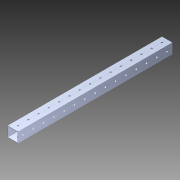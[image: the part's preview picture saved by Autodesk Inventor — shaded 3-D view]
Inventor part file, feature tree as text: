
AUTODESK INVENTOR PART (.ipt)
format: ipt  version: 2014 (Build 180170000, 170)  size: 1,226,752 bytes
history: native  units: in
note: dims shown in document units (in); Inventor stores cm internally (conversion verified against a paired STEP export)
features: pattern_circular x1, other x1, plane x1, extrude x1, imported_body x1, sketch x1
ambient origin geometry x8: Origin, YZ Plane, XZ Plane, XY Plane, X Axis, Y Axis, Z Axis, Center Point
bodies: Body1 (feature_tree)
feature tree (6):
  pattern_circular  "CirPattern2"
  other  "217-3426-STEP1"
  plane  "Work Plane1"
  extrude  "Extrusion1"  Depth=3937.0079in TaperAngle=0.0deg
  imported_body  "Base1"
  sketch  "Sketch1"  dims[d0=-15.0in d1=3937.0079in d2=0.0in]
